# Revit family: SHORT MEDIUM
name_source: partatom
category: Lighting Fixtures
units: mm (PartAtom-declared; Revit-internal decimal feet)

## family parameters
Cut with Voids When Loaded = No
Host = Face
Light Source = Yes
Maintain Annotation Orientation = Yes
Part Type = Normal
Room Calculation Point = No
Round Connector Dimension = Use Diameter
Shared = No

## types (8) — shared parameters
Color Filter = 16777215
Default Elevation = 1219 mm
Dimming Lamp Color Temperature Shift = <None>
Emit from Line Length = 610 mm
LuxLight_Alto = 112 mm
LuxLight_AltoAreaLuminosa = 30 mm
LuxLight_Amperios = 700
LuxLight_Diametro = 96 mm
LuxLight_DiametroAreaLuminosa = 70 mm
LuxLight_Watios = 28 W
Manufacturer = LUXLIGHT
Tilt Angle = 0.00°
zero-valued in all types: LuxLight_Ancho, LuxLight_AnchoAreaLuminosa, LuxLight_Largo, LuxLight_LargoAreaLuminosa, LuxLight_ProtuberanciaTecho

## per-type parameters (varying)
| type | LuxLight_Lumenes | LuxLight_Temperatura | Photometric Web File |
| LXT036M382 | 2885 lm | 2700 K | LXT036M382 .ies |
| LXT036M383 | 3054 lm | 3000 K | LXT036M383 .ies |
| LXT036M335 | 2740 lm | 3500 K | LXT036M335 .ies |
| LXT036M384 | 3232 lm | 4000 K | LXT036M384 .ies |
| LXT036M385 | 3394 lm | 5000 K | LXT036M385 .ies |
| LXT036M392 | 2262 lm | 2700 K | LXT036M392 .ies |
| LXT036M393 | 2586 lm | 3000 K | LXT036M393 .ies |
| LXT036M394 | 2909 lm | 4000 K | LXT036M394 .ies |

## geometry (parser evidence)
native form markers: Sweep x2
no freeform markers — native parametric forms only
